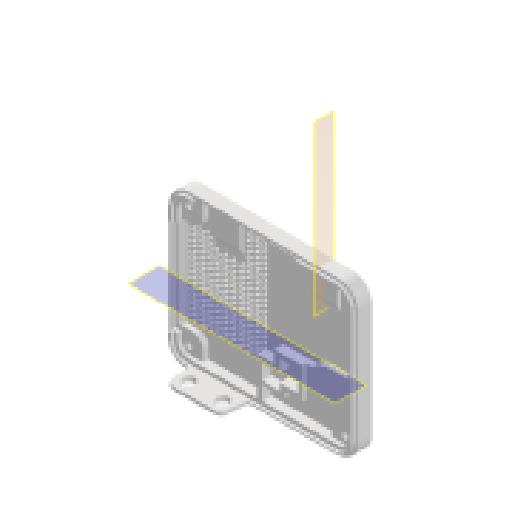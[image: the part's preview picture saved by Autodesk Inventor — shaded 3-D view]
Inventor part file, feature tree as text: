
AUTODESK INVENTOR PART (.ipt)
format: ipt  version: 2025 (Build 290162000, 162)  size: 3,189,248 bytes
history: native  units: mm
features: reference x58, sketch x28, extrude x23, other x14, fillet x6, chamfer x5, mirror x4, plane x2, shell x1, hole x1, pattern_linear x1, sweep x1
ambient origin geometry x8: Origin, YZ Plane, XZ Plane, XY Plane, X Axis, Y Axis, Z Axis, Center Point
bodies: Solid1 (feature_tree)
feature tree (144):
  extrude  "Extrusion1"  Depth=90.0mm
  extrude  "Extrusion2"  Depth=10.0mm
  shell  "Shell1"  Thickness=0.0mm
  extrude  "Extrusion8"  Depth=3.0mm
  extrude  "Extrusion9"  Depth=2.0mm
  extrude  "Extrusion10"  Depth=1.25mm
  extrude  "Extrusion11"  Depth=2.0mm TaperAngle=0.0deg
  extrude  "Extrusion13"  Depth=6.0mm
  fillet  "Fillet3"  Radius=6.0mm
  mirror  "Mirror2"
  mirror  "Mirror3"
  hole  "Hole2"  [1 undecoded]
  extrude  "Toggle_add_mat"  Depth=0.5mm
  extrude  "Toggle_hole"  Depth=3.0mm
  extrude  "Encoder_add_mat"  Depth=5.0mm
  extrude  "Encoder_hole"  Depth=4.0mm
  extrude  "Ventilation_hive"  Depth=2.625mm
  extrude  "Ventilation_vent1"  Depth=2.6mm
  extrude  "Ventilation_vent2"  Depth=1.0mm
  fillet  "Fillet4"  Radius=4.0mm
  extrude  "BTN_support"  TaperAngle=30.0deg  [1 undecoded]
  extrude  "Extrusion22"  Depth=6.0mm
  extrude  "Extrusion23"  Depth=10.0mm TaperAngle=0.0deg
  extrude  "Extrusion24"  Depth=6.0mm
  plane  "Work Plane1"
  extrude  "Extrusion27"  Depth=2.4mm
  mirror  "Mirror5"
  chamfer  "Chamfer3"  Distance=2.4mm
  extrude  "Extrusion28"  Depth=2.0mm
  chamfer  "Chamfer4"  Distance=3.6mm
  extrude  "Extrusion29"  Depth=10.0mm TaperAngle=0.0deg
  mirror  "Mirror6"
  fillet  "Fillet5"  Radius=10.0mm
  pattern_linear  "Rectangular Pattern2"  Spacing1=12.0mm  [1 undecoded]
  chamfer  "Chamfer1"  Distance=12.5mm
  fillet  "Fillet6"  Radius=3.65mm
  extrude  "Extrusion30"  Depth=0.5mm
  fillet  "Fillet7"  Radius=1.5mm
  extrude  "Extrusion31"  Depth=0.5mm TaperAngle=0.0deg
  fillet  "Fillet8"  Radius=4.0mm
  plane  "Work Plane2"
  sweep  "Sweep1"
  chamfer  "Chamfer5"  Distance=0.6mm
  chamfer  "Chamfer6"  Distance=2.5mm
  sketch  "Sketch1"  dims[d0=110.0mm d1=90.0mm]
  sketch  "Sketch2"  dims[d7=3.0mm d21=0.4mm]
  reference  "Reference1"
  reference  "Reference2"
  reference  "Reference3"
  reference  "Reference4"
  reference  "Reference5"
  reference  "Reference6"
  reference  "Reference7"
  reference  "Reference8"
  sketch  "Sketch9"  dims[d25=3.3mm d26=0.0mm d27=1.25mm]
  sketch  "Sketch10"  dims[d28=10.0mm d29=2.0mm d30=0.0mm]
  sketch  "Sketch11"  dims[d31=6.0mm d32=6.0mm d33=6.0mm]
  sketch  "Sketch12"  dims[d34=14.0mm d35=1.6mm d36=0.0mm]
  reference  "Reference38"
  reference  "Reference39"
  sketch  "Sketch16"  dims[d48=3.0mm d49=0.0mm d51=0.5mm]
  reference  "Reference49"
  sketch  "Sketch17"  dims[d52=3.3mm d53=6.0mm d54=5.75mm d55=3.2mm d56=90.0deg d57=8.0mm d58=20.594885mm d60=3.0mm]
  reference  "Reference50"
  reference  "Reference51"
  reference  "Reference52"
  sketch  "Sketch18"  dims[d63=3.0mm d64=5.0mm]
  reference  "Reference53"
  reference  "Reference54"
  reference  "Reference55"
  sketch  "Sketch19"  dims[d65=4.0mm d66=0.0mm d67=0.6mm]
  reference  "Reference56"
  reference  "Reference57"
  sketch  "Sketch20"  dims[d68=2.0mm d69=2.625mm]
  reference  "Reference58"
  sketch  "Sketch21"  dims[d70=5.45mm d71=0.0mm d72=2.6mm]
  reference  "Reference59"
  sketch  "Sketch22"  dims[d73=2.0mm d74=0.0mm d75=1.0mm d76=4.0mm d77=0.0mm]
  sketch  "Sketch Rectangular Pattern1"  dims[d2=10.0mm d3=0.0mm d4=20.0mm d5=0.0mm d6=0.0mm]
  sketch  "Sketch24"  dims[d79=38.0mm d81=30.0deg]
  reference  "Reference62"
  reference  "Reference63"
  reference  "Reference64"
  sketch  "Sketch25"  dims[d82=1.0mm d83=6.0mm]
  reference  "Reference65"
  reference  "Reference66"
  sketch  "Sketch26"  dims[d84=220.0mm d86=3.0mm d87=10.0mm d89=10.0mm d99=5.45mm d100=0.0mm]
  reference  "Reference67"
  reference  "Reference68"
  reference  "Reference69"
  reference  "Reference70"
  reference  "Reference71"
  reference  "Reference72"
  reference  "Reference73"
  reference  "Reference74"
  reference  "Reference75"
  reference  "Reference76"
  reference  "Reference77"
  reference  "Reference78"
  reference  "Reference79"
  reference  "Reference80"
  reference  "Reference81"
  reference  "Reference82"
  reference  "Reference83"
  reference  "Reference84"
  reference  "Reference85"
  reference  "Reference86"
  reference  "Reference87"
  sketch  "Sketch27"  dims[d101=2.4mm d102=0.0mm d103=6.0mm]
  sketch  "Sketch28"  dims[d104=4.0mm d105=3.5mm d106=2.4mm d107=0.0mm]
  sketch  "Sketch29"  dims[d108=2.0mm d109=2.0mm d110=45.0deg d111=1.2mm]
  sketch  "Sketch34"  dims[d112=3.0mm]
  sketch  "Sketch37"  dims[d113=2.0mm]
  reference  "Reference91"
  reference  "Reference92"
  sketch  "Sketch39"  dims[d115=0.6mm]
  reference  "Reference93"
  sketch  "Sketch40"  dims[d116=0.6mm]
  reference  "Reference94"
  reference  "Reference95"
  reference  "Reference96"
  reference  "Reference97"
  sketch  "Sketch41"  dims[d119=2.0mm]
  sketch  "Sketch Rectangular Pattern5"  dims[d22=1.7mm d23=0.0mm d24=2.0mm]
  sketch  "Sketch42"  dims[d120=3.5mm d121=3.6mm d122=10.0mm d123=0.0mm d124=10.0mm d125=0.0mm d126=12.0mm d127=12.5mm d129=3.65mm d130=0.0mm d131=2.5mm d134=1.5mm d135=0.0mm d158=2.6mm d159=0.0mm d163=4.0mm d164=16.0mm d166=0.6mm d169=2.5mm d170=0.15mm d171=11.34464mm d174=3.0mm d175=2.0mm d176=60.0deg d178=4.0mm d179=2.0mm d180=0.0mm d181=2.0mm d182=2.0mm d183=60.0deg d187=0.45mm d189=2.42mm d191=1.5mm d192=1.4505mm d193=0.4mm d194=2.8mm d195=150.0deg d196=10.0mm d197=0.0mm d198=2.0mm d199=1.35mm d200=2.0mm d201=20.0mm d203=55.0mm d204=3.0mm d206=7.5mm d207=0.9mm d208=3.3mm d209=5.0mm d211=20.0mm d220=3.0mm d221=14.835299mm d223=19.05mm d224=2.8mm d225=0.0mm d226=4.0mm d227=1.0mm d228=2.8mm d229=0.0mm d230=2.0mm d239=20.0mm d241=3.0mm d242=130.0mm d244=5.0mm d247=0.0mm d248=0.0mm d249=0.3mm d250=2.0mm d251=45.0deg d252=0.5mm d253=2.0mm d254=45.0deg d231=0.5mm d232=0.872665mm d233=0.5mm d234=0.872665mm]
  reference  "Reference98"
  reference  "Reference99"
  reference  "Reference100"
  reference  "Reference101"
  sketch  "3D Sketch1"
  other  "USB_C_PD_PPS_sink_with_enclosure.iam"
  other  "top_enclosure:1"
  other  "USB_C_PD_PPS_sink:1"
  other  "USB-MICRO-B_V_CMP-2000-05827-1:1"
  other  "FP-USB4085-GF-A-MFG_USB4085-GF-A-1:1"
  other  "USB_C_PD_PPS_sink_BOARD:1"
  other  "1M41T1B5M1QE_1M41T1B5M1QE-1:1"
  other  "Aluminium_knob:1"
  other  "B3F-1075_CMP-003-000047-3:1"
  other  "B3F-1075_CMP-003-000047-3:2"
  other  "B3F-1052_B3F-1052-1:2"
  other  "B3F-1052_B3F-1052-1:1"
  other  "B3F-1052_B3F-1052-1:3"
  other  "tilt_leg:1"
note: 3 required parameter values undecoded (feature->parameter linkage not recoverable at this tier; creation-order binding heuristic only, values carry confidence <= 0.55)
